FCSTD DOCUMENT  (FreeCAD 0.17R13522 (Git))
Label: usbled
License: CreativeCommons Attribution-ShareAlike
LicenseURL: http://creativecommons.org/licenses/by-sa/4.0/
objects: Sketcher::SketchObject×1, PartDesign::Body×1, App::Part×1
note: 2 computed .brp shape members not serialized (recipe doc carries the construction recipe); baked Part::Feature solids carry a one-line shape summary decoded from their .brp

FEATURE [Sketcher::SketchObject] Sketch
  MapMode = 5
  Support = -> [XY_Plane001]
  sketch-geometry (10):
    g0: LineSegment StartX=1 StartY=6.03 StartZ=0 EndX=23 EndY=6.03 EndZ=0
    g1: LineSegment StartX=25 StartY=4.03 StartZ=0 EndX=25 EndY=-4.03 EndZ=0
    g2: LineSegment StartX=23 StartY=-6.03 StartZ=0 EndX=1 EndY=-6.03 EndZ=0
    g3: LineSegment StartX=0 StartY=-5.03 StartZ=0 EndX=0 EndY=5.03 EndZ=0
    g4: ArcOfCircle CenterX=23 CenterY=4.03 CenterZ=0 NormalX=0 NormalY=0 NormalZ=1 AngleXU=0 Radius=2 StartAngle=-4e-12 EndAngle=1.5708
    g5: ArcOfCircle CenterX=23 CenterY=-4.03 CenterZ=0 NormalX=0 NormalY=0 NormalZ=1 AngleXU=0 Radius=2 StartAngle=4.71239 EndAngle=6.28319
    g6: LineSegment [constr] StartX=23 StartY=6.03 StartZ=0 EndX=23 EndY=-6.03 EndZ=0
    g7: ArcOfCircle CenterX=1 CenterY=5.03 CenterZ=0 NormalX=0 NormalY=0 NormalZ=1 AngleXU=0 Radius=1 StartAngle=1.5708 EndAngle=3.14159
    g8: ArcOfCircle CenterX=1 CenterY=-5.03 CenterZ=0 NormalX=0 NormalY=0 NormalZ=1 AngleXU=0 Radius=1 StartAngle=3.14159 EndAngle=4.71239
    g9: LineSegment [constr] StartX=1 StartY=6.03 StartZ=0 EndX=1 EndY=-6.03 EndZ=0
  constraints (23):
    c: Horizontal(g0)
    c: Horizontal(g2)
    c: Vertical(g3)
    c: Tangent(g0,g4) = 1.5708
    c: Tangent(g1,g4) = 1.5708
    c: Tangent(g1,g5) = 1.5708
    c: Tangent(g2,g5) = 1.5708
    c: Coincident(g6,g0)
    c: Coincident(g6,g2)
    c: Vertical(g6)
    c: Symmetric(g1,g1,g-1)
    c: Tangent(g0,g7) = 1.5708
    c: Tangent(g3,g7) = 1.5708
    c: Tangent(g2,g8) = 1.5708
    c: Tangent(g3,g8) = 1.5708
    c: PointOnObject(g3,g-2)
    c: Coincident(g9,g0)
    c: Coincident(g9,g2)
    c: Vertical(g9)
    c: Radius(g8) = 1
    c: Radius(g4) = 2
    c: DistanceX(g1) = 25
    c: DistanceY(g9,g9) = 12.06
FEATURE [PartDesign::Body] Body
  Group = -> [Sketch]
  Origin = -> Origin001
FEATURE [App::Part] Part
  Group = -> [Body]
  License = CC BY 3.0
  LicenseURL = http://creativecommons.org/licenses/by/3.0/
  Origin = -> Origin
